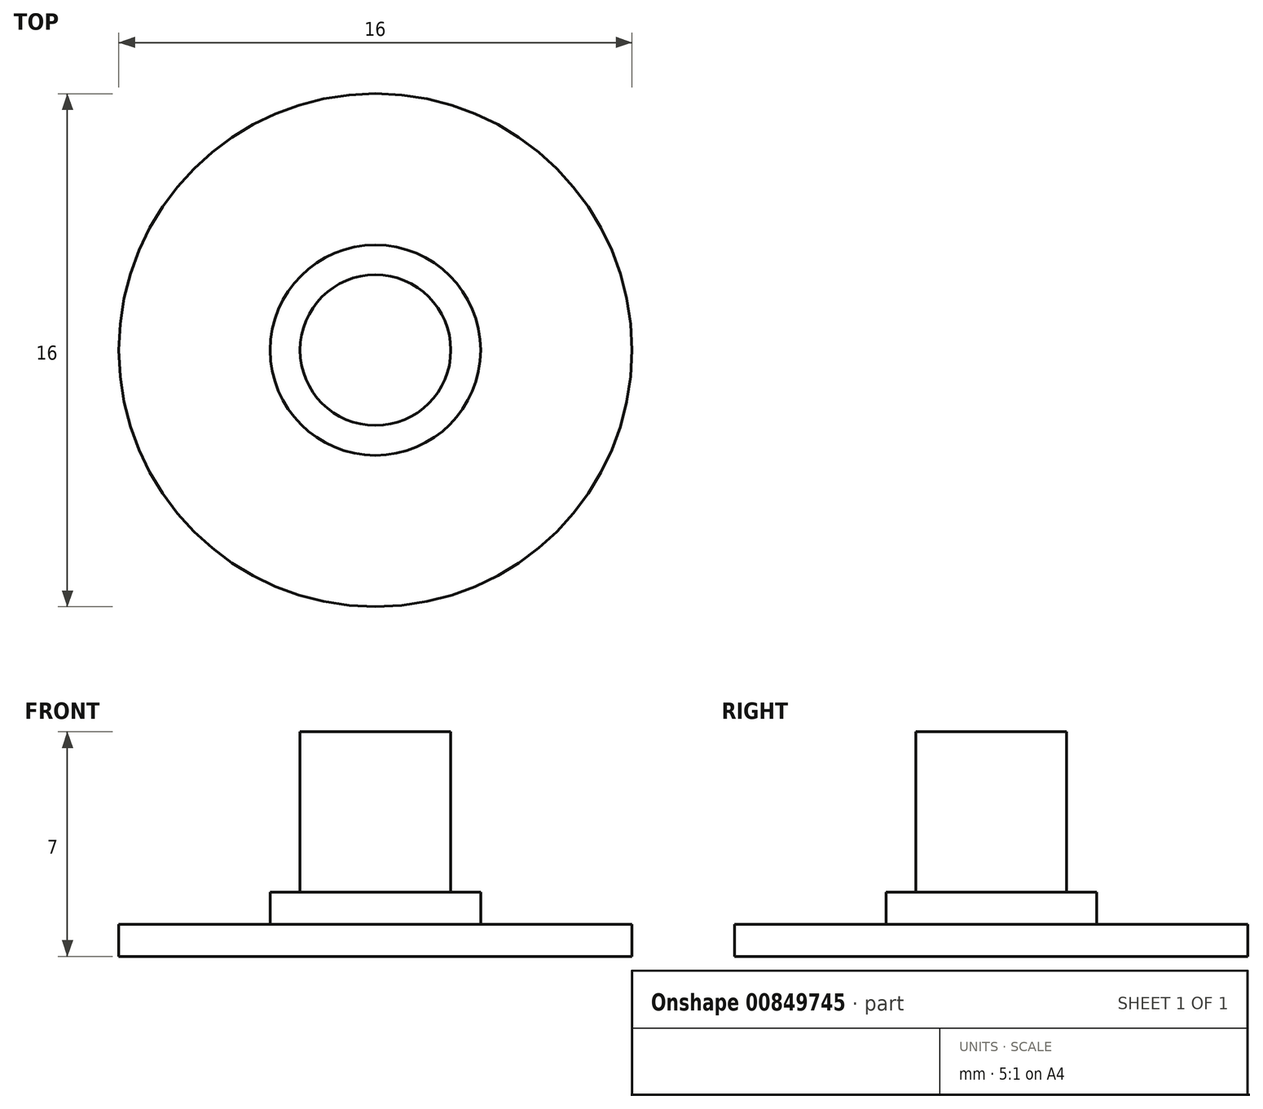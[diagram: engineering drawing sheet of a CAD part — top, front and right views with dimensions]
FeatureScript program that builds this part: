
annotation { "Feature Type Name" : "Feature", "Feature Type Description" : "" }
export const myFeature = defineFeature(function(context is Context, id is Id, definition is map)
    precondition{}
    {
        {
            var Q0;
            Q0=qCreatedBy(makeId("Top.planeOp"),FACE);
            var sketch = newSketch(context, id + "F0", { "sketchPlane" : qUnion([Q0])});
            skCircle(sketch, "E0", {"center": v(0, 0) * mm, "radius": 8.15 * mm});
            skCircle(sketch, "E1", {"center": v(0, 0) * mm, "radius": 13.15 * mm});
            skCircle(sketch, "E2.cCircle", {"center": v(30.96, 0) * mm, "radius": 8.5 * mm, "construction": true});
            skLineSegment(sketch, "E2.0", {"start": v(26.06, 8.5) * mm, "end": v(35.87, 8.5) * mm});
            skLineSegment(sketch, "E2.1", {"start": v(35.87, 8.5) * mm, "end": v(40.78, 0) * mm});
            skLineSegment(sketch, "E2.2", {"start": v(40.78, 0) * mm, "end": v(35.87, -8.5) * mm});
            skLineSegment(sketch, "E2.3", {"start": v(35.87, -8.5) * mm, "end": v(26.06, -8.5) * mm});
            skLineSegment(sketch, "E2.4", {"start": v(26.06, -8.5) * mm, "end": v(21.15, 0) * mm});
            skLineSegment(sketch, "E2.5", {"start": v(21.15, 0) * mm, "end": v(26.06, 8.5) * mm});
            skPoint(sketch, "E2.0.midPoint", {"position": v(30.96, 8.5) * mm});
            skCircle(sketch, "E3.cCircle", {"center": v(-30.96, 0) * mm, "radius": 8.5 * mm, "construction": true});
            skLineSegment(sketch, "E3.0", {"start": v(-35.87, 8.5) * mm, "end": v(-26.06, 8.5) * mm});
            skLineSegment(sketch, "E3.1", {"start": v(-26.06, 8.5) * mm, "end": v(-21.15, 0) * mm});
            skLineSegment(sketch, "E3.2", {"start": v(-21.15, 0) * mm, "end": v(-26.06, -8.5) * mm});
            skLineSegment(sketch, "E3.3", {"start": v(-26.06, -8.5) * mm, "end": v(-35.87, -8.5) * mm});
            skLineSegment(sketch, "E3.4", {"start": v(-35.87, -8.5) * mm, "end": v(-40.78, 0) * mm});
            skLineSegment(sketch, "E3.5", {"start": v(-40.78, 0) * mm, "end": v(-35.87, 8.5) * mm});
            skPoint(sketch, "E3.0.midPoint", {"position": v(-30.96, 8.5) * mm});
            skLineSegment(sketch, "E4", {"start": v(-21.15, 0) * mm, "end": v(-13.15, 0) * mm});
            skLineSegment(sketch, "E5", {"start": v(13.15, 0) * mm, "end": v(21.15, 0) * mm});
            skCircle(sketch, "E6", {"center": v(30.96, 0) * mm, "radius": 12.89 * mm});
            skCircle(sketch, "E7", {"center": v(-30.96, 0) * mm, "radius": 12.89 * mm});
            skArc(sketch, "E8", {"start": v(-26.44, 12.07) * mm, "mid": v(-16.13, 9.67) * mm, "end": v(-5.77, 11.82) * mm});
            skArc(sketch, "E9", {"start": v(4.97, 12.17) * mm, "mid": v(15.37, 9.68) * mm, "end": v(25.85, 11.83) * mm});
            skArc(sketch, "E10", {"start": v(-6.08, -11.66) * mm, "mid": v(-15.97, -10.23) * mm, "end": v(-25.83, -11.82) * mm});
            skArc(sketch, "E11", {"start": v(25.56, -11.64) * mm, "mid": v(15.68, -10.2) * mm, "end": v(5.81, -11.8) * mm});
            skSolve(sketch);
        }
        {
            var Q0;
            Q0=qCreatedBy(makeId("Top.planeOp"),FACE);
            var sketch = newSketch(context, id + "F1", { "sketchPlane" : qUnion([Q0])});
            skCircle(sketch, "E12", {"center": v(0, 28.16) * mm, "radius": 2.35 * mm});
            skCircle(sketch, "E13", {"center": v(0, 28.16) * mm, "radius": 8 * mm});
            skSolve(sketch);
        }
        {
            var Q0;
            Q0=makeQuery(id+"F1.imprint","IMPRINT",FACE,{"disambiguationData":[TD([[makeQuery(id+"F1.imprint","IMPRINT",EDGE,{"derivedFrom":sQuery(id+"F1.wireOp",EDGE,"E12")}),-1.0]])]});
            var Q1;
            Q1=makeQuery(id+"F1.imprint","IMPRINT",FACE,{"disambiguationData":[TD([[makeQuery(id+"F1.imprint","IMPRINT",EDGE,{"derivedFrom":sQuery(id+"F1.wireOp",EDGE,"E12")}),1.0]])]});
            extrude(context, id + "F2", {"entities" : qUnion([Q0, Q1]), "depth" : 1 * mm, "offsetDistance" : 25.4 * mm});
        }
        {
            var Q0;
            Q0=makeQuery(id+"F1.imprint","IMPRINT",FACE,{"disambiguationData":[TD([[makeQuery(id+"F1.imprint","IMPRINT",EDGE,{"derivedFrom":sQuery(id+"F1.wireOp",EDGE,"E12")}),1.0]])]});
            var Q1;
            Q1=makeQuery(id+"FNYiAPRMe3rHjbK_0.opExtrude","CAP_FACE",FACE,{"disambiguationData":[OSD([sQuery(id+"F0.wireOp",EDGE,"E0"),sQuery(id+"F0.wireOp",EDGE,"E1"),sQuery(id+"F0.wireOp",EDGE,"E2.0"),sQuery(id+"F0.wireOp",EDGE,"E2.1"),sQuery(id+"F0.wireOp",EDGE,"E2.2"),sQuery(id+"F0.wireOp",EDGE,"E2.3"),sQuery(id+"F0.wireOp",EDGE,"E2.4"),sQuery(id+"F0.wireOp",EDGE,"E2.5"),sQuery(id+"F0.wireOp",EDGE,"E3.0"),sQuery(id+"F0.wireOp",EDGE,"E3.1"),sQuery(id+"F0.wireOp",EDGE,"E3.2"),sQuery(id+"F0.wireOp",EDGE,"E3.3"),sQuery(id+"F0.wireOp",EDGE,"E3.4"),sQuery(id+"F0.wireOp",EDGE,"E3.5"),sQuery(id+"F0.wireOp",EDGE,"E6"),sQuery(id+"F0.wireOp",EDGE,"E7"),sQuery(id+"F0.wireOp",EDGE,"E8"),sQuery(id+"F0.wireOp",EDGE,"E9"),sQuery(id+"F0.wireOp",EDGE,"E10"),sQuery(id+"F0.wireOp",EDGE,"E11")])],"isStart":false});
            extrude(context, id + "F3", {"entities" : qUnion([Q0]), "operationType" : NewBodyOperationType.ADD, "depth" : 7 * mm, "endBoundEntityFace" : qUnion([Q1]), "offsetDistance" : 25.4 * mm});
        }
        {
            var Q0;
            Q0=makeQuery(id+"F1.imprint","IMPRINT",FACE,{"disambiguationData":[TD([[makeQuery(id+"F1.imprint","IMPRINT",EDGE,{"derivedFrom":sQuery(id+"F1.wireOp",EDGE,"E12")}),-1.0]])]});
            var Q1;
            Q1=makeQuery(id+"F1.imprint","IMPRINT",FACE,{"disambiguationData":[TD([[makeQuery(id+"F1.imprint","IMPRINT",EDGE,{"derivedFrom":sQuery(id+"F1.wireOp",EDGE,"E12")}),1.0]])]});
            extrude(context, id + "F4", {"entities" : qUnion([Q0, Q1]), "oppositeDirection" : true, "depth" : 1.1 * mm, "offsetDistance" : 25.4 * mm, "hasSecondDirection" : true, "secondDirectionOppositeDirection" : true, "secondDirectionDepth" : 0.1 * mm});
        }
        {
            var Q0;
            Q0=makeQuery(id+"F4.opExtrude","SWEPT_BODY",BODY,{"disambiguationData":[OSD([sQuery(id+"F1.wireOp",EDGE,"E13")])]});
            transform(context, id + "F5", {"entities" : qUnion([Q0]), "transformType" : TransformType.TRANSLATION_3D, "dx" : -18.77 * mm, "dy" : 0 * mm, "dz" : 1.1 * mm, "makeCopy" : false});
        }
        {
            var Q0;
            Q0=makeQuery(id+"F4.opExtrude","SWEPT_BODY",BODY,{"disambiguationData":[OSD([sQuery(id+"F1.wireOp",EDGE,"E13")])]});
            deleteBodies(context, id + "F6", {"entities" : qUnion([Q0])});
        }
        {
            var Q0;
            Q0=makeQuery(id+"F2.opExtrude","CAP_FACE",FACE,{"disambiguationData":[OSD([sQuery(id+"F1.wireOp",EDGE,"E13")])],"isStart":false});
            var sketch = newSketch(context, id + "F7", { "sketchPlane" : qUnion([Q0])});
            skCircle(sketch, "E14", {"center": v(0, 28.16) * mm, "radius": 3.28 * mm});
            skSolve(sketch);
        }
        {
            var Q0;
            Q0=makeQuery(id+"F7.imprint","IMPRINT",FACE,{"disambiguationData":[TD([[makeQuery(id+"F7.imprint","IMPRINT",EDGE,{"derivedFrom":sQuery(id+"F7.wireOp",EDGE,"E14")}),1.0]])]});
            extrude(context, id + "F8", {"entities" : qUnion([Q0]), "operationType" : NewBodyOperationType.ADD, "depth" : 1 * mm, "offsetDistance" : 25.4 * mm});
        }
    });
